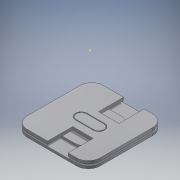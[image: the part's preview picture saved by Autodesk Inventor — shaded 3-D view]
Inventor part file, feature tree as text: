
AUTODESK INVENTOR PART (.ipt)
format: ipt  version: 2017 (Build 210142000, 142)  size: 1,430,016 bytes
history: native  units: mm
features: other x18, extrude x11, sketch x8, thicken_offset x5, projected_geometry x5, move_body x5, fillet x3, shell x2, plane x2, direct_edit x2, mirror x1, split x1
ambient origin geometry x8: Origin, YZ Plane, XZ Plane, XY Plane, X Axis, Y Axis, Z Axis, Center Point
bodies: Body1 (feature_tree), Body2 (feature_tree), Body3 (feature_tree), Body4 (feature_tree), Body5 (feature_tree)
feature tree (63):
  other  "Frame.ipt"
  shell  "Shell_bottom_plane"  Thickness=10.0mm
  sketch  "Sketch2"  dims[d12=-2.5mm d13=55.88mm]
  extrude  "Extrusion2"  Depth=55.88mm
  extrude  "Extrusion3"  Depth=33.0mm TaperAngle=0.0deg
  extrude  "Extrusion21"  Depth=1.5mm
  extrude  "Extrusion7"  Depth=5.0mm
  fillet  "Fillet6"  Radius=1.5mm
  mirror  "Mirror1"
  sketch  "Sketch12"  dims[d18=25.25mm d19=0.0mm d54=1.5mm]
  extrude  "Extrusion12"  Depth=4.0mm
  sketch  "Sketch13"  dims[d55=0.5mm d56=5.0mm d57=1.5mm]
  extrude  "Extrusion13"  Depth=0.5mm
  fillet  "Fillet9"  Radius=8.0mm
  plane  "Work Plane9"
  extrude  "Extrusion29"  Depth=3.175mm
  split  "Split2"
  direct_edit  "Direct Edit5"
  plane  "Work Plane10"
  sketch  "Sketch26"  dims[d78=0.5mm d83=9.525mm d89=1.0mm d90=4.0mm d91=0.0mm d92=0.508mm d97=32.0mm d98=0.0mm d117=16.175mm d118=5.2625mm d119=0.0mm d120=1.5mm d121=3.175mm d122=3.175mm d123=4.175mm d124=10.0mm d167=1.6mm d168=26.0mm d169=1.0mm d170=0.0mm d171=7.0mm d173=0.6mm d174=4.0mm d175=6.0mm d176=5.0mm d177=0.6mm d178=0.0mm d179=0.8mm d180=0.0mm d181=1.0mm d182=0.0mm d183=1.0mm d184=0.0mm d188=0.0mm d189=0.0mm d190=0.6mm d191=0.2mm d192=0.2mm d193=0.2mm d194=0.2mm d195=0.2mm d196=0.2mm d197=0.2mm d198=0.2mm d199=4.0mm d200=0.3mm d201=0.3mm d202=5.0mm d203=0.0mm d204=0.0mm d205=-1.6mm d206=0.0mm d207=0.0mm d208=-1.6mm d214=0.0mm d215=0.0mm d216=-0.5mm d217=0.0mm d218=0.0mm d219=-0.5mm d221=0.8mm]
  extrude  "Extrusion32"  Depth=0.8mm
  extrude  "Extrusion30"  Depth=1.0mm
  extrude  "Extrusion31"  Depth=4.0mm TaperAngle=0.0deg
  extrude  "Extrusion33"  Depth=0.8mm
  thicken_offset  "Thicken2"
  thicken_offset  "Thicken3"
  thicken_offset  "Thicken4"
  thicken_offset  "Thicken5"
  thicken_offset  "Thicken6"
  fillet  "Fillet11"  Radius=32.0mm
  direct_edit  "Direct Edit6"
  other  "TaggingFeature1"
  shell  "Shell"  Thickness=16.175mm
  other  "Bottom_board::Frame.ipt"
  other  "Motor_R::Frame.ipt"
  other  "Wheel_R::Frame.ipt"
  other  "Bottom_board_connectors::Frame.ipt"
  other  "Motor_L::Frame.ipt"
  other  "Wheel_L::Frame.ipt"
  other  "Top_board::Frame.ipt"
  other  "Top_board_connectors::Frame.ipt"
  other  "WiFi_board::Frame.ipt"
  sketch  "Sketch7"  dims[d14=1.0mm d15=33.0mm d16=0.0mm]
  projected_geometry  "Projected Loop4"
  projected_geometry  "Projected Loop5"
  projected_geometry  "Projected Loop6"
  projected_geometry  "Projected Loop7"
  projected_geometry  "Projected Loop11"
  sketch  "Sketch18"  dims[d60=1.5mm d61=0.5mm d62=8.0mm]
  other  "Charging_frame_R::Frame.ipt_1"
  other  "Charging_frame_L::Frame.ipt_1"
  other  "TaggingFeature2"
  sketch  "Sketch17"  dims[d58=0.5mm d59=4.0mm]
  sketch  "Sketch25"  dims[d63=10.0mm d64=0.0mm d65=3.175mm]
  other  "Charging_frame_cap"
  other  "Charging_frame_base"
  other  "Charging_frame"
  other  "Frame"
  move_body  "Move6"
  move_body  "Move7"
  move_body  "Move8"
  move_body  "Move9"
  move_body  "Move10"
